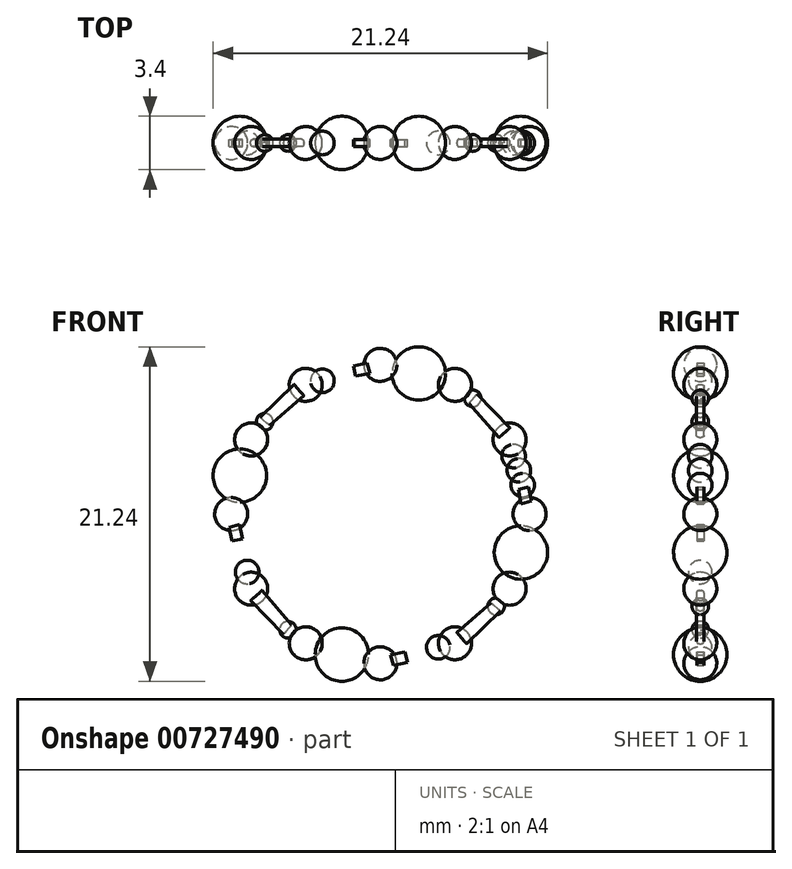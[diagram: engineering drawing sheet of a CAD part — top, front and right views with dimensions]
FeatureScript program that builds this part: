
annotation { "Feature Type Name" : "Feature", "Feature Type Description" : "" }
export const myFeature = defineFeature(function(context is Context, id is Id, definition is map)
    precondition{}
    {
        {
            var Q0;
            Q0=qCreatedBy(makeId("Front.planeOp"),FACE);
            var sketch = newSketch(context, id + "F0", { "sketchPlane" : qUnion([Q0])});
            skCircle(sketch, "E0", {"center": v(0, 0) * mm, "radius": 9 * mm});
            skSolve(sketch);
        }
        {
            var Q0;
            Q0=qCreatedBy(makeId("Front.planeOp"),FACE);
            var sketch = newSketch(context, id + "F1", { "sketchPlane" : qUnion([Q0])});
            skCircle(sketch, "E1", {"center": v(9.48, 0) * mm, "radius": 1.05 * mm});
            skLineSegment(sketch, "E2", {"start": v(9.48, 2.02) * mm, "end": v(9.48, -1.54) * mm});
            skSolve(sketch);
        }
        {
            var Q0;
            {var subQ0=sQuery(id+"F1.wireOp",EDGE,"E2");var subQ1=sQuery(id+"F1.wireOp",EDGE,"E1");var subQ2=makeQuery(id+"F1.imprint","INTERSECT",VERTEX,{"disambiguationData":[OD(0.0)],"derivedFrom":[subQ1,subQ0]});Q0=makeQuery(id+"F1.imprint","IMPRINT",FACE,{"disambiguationData":[TD([[makeQuery(id+"F1.imprint","IMPRINT",EDGE,{"disambiguationData":[TD([[subQ2,1.0]])],"derivedFrom":subQ1}),1.0]])]});}
            var Q1;
            Q1=sQuery(id+"F1.wireOp",EDGE,"E2");
            revolve(context, id + "F2", {"surfaceOperationType" : NewSurfaceOperationType.NEW, "entities" : qUnion([Q0]), "axis" : qUnion([Q1]), "revolveType" : RevolveType.FULL});
        }
        {
            var Q0;
            Q0=makeQuery(id+"F2.opRevolve","SWEPT_BODY",BODY,{"disambiguationData":[OSD([sQuery(id+"F1.wireOp",EDGE,"E1"),sQuery(id+"F1.wireOp",EDGE,"E2")])]});
            var Q1;
            Q1=sQuery(id+"F0.wireOp",EDGE,"E0");
            circularPattern(context, id + "F3", {"entities" : qUnion([Q0]), "axis" : qUnion([Q1]), "angle" : 360 * degree, "instanceCount" : 12, "equalSpace" : true});
        }
        {
            var Q0;
            Q0=qCreatedBy(makeId("Front.planeOp"),FACE);
            var sketch = newSketch(context, id + "F4", { "sketchPlane" : qUnion([Q0])});
            skCircle(sketch, "E3", {"center": v(8.93, -2.44) * mm, "radius": 1.7 * mm});
            skLineSegment(sketch, "E4", {"start": v(8.93, -0.4) * mm, "end": v(8.93, -5.01) * mm});
            skSolve(sketch);
        }
        {
            var Q0;
            {var subQ0=sQuery(id+"F4.wireOp",EDGE,"E4");var subQ1=sQuery(id+"F4.wireOp",EDGE,"E3");var subQ2=makeQuery(id+"F4.imprint","INTERSECT",VERTEX,{"disambiguationData":[OD(0.0)],"derivedFrom":[subQ1,subQ0]});Q0=makeQuery(id+"F4.imprint","IMPRINT",FACE,{"disambiguationData":[TD([[makeQuery(id+"F4.imprint","IMPRINT",EDGE,{"disambiguationData":[TD([[subQ2,1.0]])],"derivedFrom":subQ1}),1.0]])]});}
            var Q1;
            Q1=sQuery(id+"F4.wireOp",EDGE,"E4");
            revolve(context, id + "F5", {"surfaceOperationType" : NewSurfaceOperationType.NEW, "entities" : qUnion([Q0]), "axis" : qUnion([Q1]), "revolveType" : RevolveType.FULL});
        }
        {
            var Q0;
            Q0=qCreatedBy(makeId("Front.planeOp"),FACE);
            var sketch = newSketch(context, id + "F6", { "sketchPlane" : qUnion([Q0])});
            skCircle(sketch, "E5", {"center": v(9.04, 1.84) * mm, "radius": 0.75 * mm});
            skLineSegment(sketch, "E6", {"start": v(9.04, 2.84) * mm, "end": v(9.04, 0.4) * mm});
            skSolve(sketch);
        }
        {
            var Q0;
            {var subQ0=sQuery(id+"F6.wireOp",EDGE,"E6");var subQ1=sQuery(id+"F6.wireOp",EDGE,"E5");var subQ2=makeQuery(id+"F6.imprint","INTERSECT",VERTEX,{"disambiguationData":[OD(0.0)],"derivedFrom":[subQ1,subQ0]});Q0=makeQuery(id+"F6.imprint","IMPRINT",FACE,{"disambiguationData":[TD([[makeQuery(id+"F6.imprint","IMPRINT",EDGE,{"disambiguationData":[TD([[subQ2,1.0]])],"derivedFrom":subQ1}),1.0]])]});}
            var Q1;
            Q1=sQuery(id+"F6.wireOp",EDGE,"E6");
            revolve(context, id + "F7", {"operationType" : NewBodyOperationType.ADD, "surfaceOperationType" : NewSurfaceOperationType.NEW, "entities" : qUnion([Q0]), "axis" : qUnion([Q1]), "revolveType" : RevolveType.FULL});
        }
        {
            var Q0;
            Q0=makeQuery(id+"F5.opRevolve","SWEPT_BODY",BODY,{"disambiguationData":[OSD([sQuery(id+"F4.wireOp",EDGE,"E3"),sQuery(id+"F4.wireOp",EDGE,"E4")])]});
            var Q1;
            Q1=sQuery(id+"F0.wireOp",EDGE,"E0");
            circularPattern(context, id + "F8", {"entities" : qUnion([Q0]), "axis" : qUnion([Q1]), "angle" : 360 * degree, "instanceCount" : 4, "equalSpace" : true});
        }
        {
            var Q0;
            Q0=makeQuery(id+"F7.opRevolve","SWEPT_BODY",BODY,{"disambiguationData":[OSD([sQuery(id+"F6.wireOp",EDGE,"E5"),sQuery(id+"F6.wireOp",EDGE,"E6")])]});
            var Q1;
            Q1=sQuery(id+"F0.wireOp",EDGE,"E0");
            circularPattern(context, id + "F9", {"entities" : qUnion([Q0]), "axis" : qUnion([Q1]), "angle" : 12 * degree, "instanceCount" : 3, "equalSpace" : true});
        }
        {
            var Q0;
            Q0=makeQuery(id+"F9.opPattern","COPY",BODY,{"derivedFrom":makeQuery(id+"F7.opRevolve","SWEPT_BODY",BODY,{"disambiguationData":[OSD([sQuery(id+"F6.wireOp",EDGE,"E5"),sQuery(id+"F6.wireOp",EDGE,"E6")])]}),"instanceName":"2"});
            var Q1;
            Q1=sQuery(id+"F0.wireOp",EDGE,"E0");
            circularPattern(context, id + "F10", {"entities" : qUnion([Q0]), "axis" : qUnion([Q1]), "angle" : 360 * degree, "instanceCount" : 4, "equalSpace" : true});
        }
        {
            var Q0;
            Q0=qCreatedBy(makeId("Front.planeOp"),FACE);
            var sketch = newSketch(context, id + "F11", { "sketchPlane" : qUnion([Q0])});
            skCircle(sketch, "E7", {"center": v(7.35, -5.86) * mm, "radius": 0.53 * mm});
            skLineSegment(sketch, "E8", {"start": v(7.35, -4.97) * mm, "end": v(7.35, -6.96) * mm});
            skSolve(sketch);
        }
        {
            var Q0;
            {var subQ0=sQuery(id+"F11.wireOp",EDGE,"E8");var subQ1=sQuery(id+"F11.wireOp",EDGE,"E7");var subQ2=makeQuery(id+"F11.imprint","INTERSECT",VERTEX,{"disambiguationData":[OD(0.0)],"derivedFrom":[subQ1,subQ0]});Q0=makeQuery(id+"F11.imprint","IMPRINT",FACE,{"disambiguationData":[TD([[makeQuery(id+"F11.imprint","IMPRINT",EDGE,{"disambiguationData":[TD([[subQ2,-1.0]])],"derivedFrom":subQ1}),1.0]])]});}
            var Q1;
            Q1=sQuery(id+"F11.wireOp",EDGE,"E8");
            revolve(context, id + "F12", {"operationType" : NewBodyOperationType.ADD, "surfaceOperationType" : NewSurfaceOperationType.NEW, "entities" : qUnion([Q0]), "axis" : qUnion([Q1]), "revolveType" : RevolveType.FULL});
        }
        {
            var Q0;
            Q0=makeQuery(id+"F3.opPattern","COPY",BODY,{"derivedFrom":makeQuery(id+"F2.opRevolve","SWEPT_BODY",BODY,{"disambiguationData":[OSD([sQuery(id+"F1.wireOp",EDGE,"E1"),sQuery(id+"F1.wireOp",EDGE,"E2")])]}),"instanceName":"11"});
            var Q1;
            Q1=sQuery(id+"F0.wireOp",EDGE,"E0");
            circularPattern(context, id + "F13", {"entities" : qUnion([Q0]), "axis" : qUnion([Q1]), "angle" : 360 * degree, "instanceCount" : 4, "equalSpace" : true});
        }
        {
            var Q0;
            Q0=qCreatedBy(makeId("Front.planeOp"),FACE);
            var sketch = newSketch(context, id + "F14", { "sketchPlane" : qUnion([Q0])});
            skLineSegment(sketch, "E9", {"start": v(-5.64, -7.03) * mm, "end": v(-7.53, -4.86) * mm});
            skLineSegment(sketch, "E10", {"start": v(-7.53, -4.86) * mm, "end": v(-8.23, -5.48) * mm});
            skLineSegment(sketch, "E11", {"start": v(-8.23, -5.48) * mm, "end": v(-6.15, -7.64) * mm});
            skLineSegment(sketch, "E12", {"start": v(-6.15, -7.64) * mm, "end": v(-5.64, -7.03) * mm});
            skSolve(sketch);
        }
        {
            var Q0;
            Q0 = qSketchRegion(id + "F14", true);
            extrude(context, id + "F15", {"entities" : qUnion([Q0]), "endBound" : BoundingType.SYMMETRIC, "depth" : 0.48 * mm, "offsetDistance" : 25 * mm});
        }
        {
            var Q0;
            Q0=makeQuery(id+"F15.opExtrude","CAP_EDGE",EDGE,{"disambiguationData":[OSD([sQuery(id+"F14.wireOp",EDGE,"E9")])],"isStart":false});
            var Q1;
            Q1=makeQuery(id+"F15.opExtrude","CAP_EDGE",EDGE,{"disambiguationData":[OSD([sQuery(id+"F14.wireOp",EDGE,"E11")])],"isStart":false});
            var Q2;
            Q2=makeQuery(id+"F15.opExtrude","CAP_EDGE",EDGE,{"disambiguationData":[OSD([sQuery(id+"F14.wireOp",EDGE,"E9")])],"isStart":true});
            var Q3;
            Q3=makeQuery(id+"F15.opExtrude","CAP_EDGE",EDGE,{"disambiguationData":[OSD([sQuery(id+"F14.wireOp",EDGE,"E11")])],"isStart":true});
            fillet(context, id + "F16", {"entities" : qUnion([Q0, Q1, Q2, Q3]), "radius" : .2 * mm, "tangentPropagation" : true, "allowEdgeOverflow" : false});
        }
        {
            var Q0;
            Q0=makeQuery(id+"F15.opExtrude","SWEPT_BODY",BODY,{"disambiguationData":[OSD([sQuery(id+"F14.wireOp",EDGE,"E9"),sQuery(id+"F14.wireOp",EDGE,"E10"),sQuery(id+"F14.wireOp",EDGE,"E11"),sQuery(id+"F14.wireOp",EDGE,"E12")])]});
            var Q1;
            Q1=sQuery(id+"F0.wireOp",EDGE,"E0");
            circularPattern(context, id + "F17", {"entities" : qUnion([Q0]), "axis" : qUnion([Q1]), "angle" : 360 * degree, "instanceCount" : 4, "equalSpace" : true});
        }
        {
            var Q0;
            Q0=qCreatedBy(makeId("Front.planeOp"),FACE);
            var sketch = newSketch(context, id + "F18", { "sketchPlane" : qUnion([Q0])});
            skLineSegment(sketch, "E13", {"start": v(-9.6, -0.83) * mm, "end": v(-9.4, -1.72) * mm});
            skLineSegment(sketch, "E14", {"start": v(-8.77, -1.57) * mm, "end": v(-9.4, -1.72) * mm});
            skLineSegment(sketch, "E15", {"start": v(-8.94, -0.66) * mm, "end": v(-8.77, -1.57) * mm});
            skLineSegment(sketch, "E16", {"start": v(-9.6, -0.83) * mm, "end": v(-8.94, -0.66) * mm});
            skSolve(sketch);
        }
        {
            var Q0;
            Q0=makeQuery(id+"F18.imprint","IMPRINT",FACE,{"disambiguationData":[TD([[makeQuery(id+"F18.imprint","IMPRINT",EDGE,{"derivedFrom":sQuery(id+"F18.wireOp",EDGE,"E13")}),1.0]])]});
            extrude(context, id + "F19", {"entities" : qUnion([Q0]), "endBound" : BoundingType.SYMMETRIC, "depth" : 0.44 * mm, "offsetDistance" : 25 * mm});
        }
        {
            var Q0;
            Q0=makeQuery(id+"F19.opExtrude","SWEPT_BODY",BODY,{"disambiguationData":[OSD([sQuery(id+"F18.wireOp",EDGE,"E13"),sQuery(id+"F18.wireOp",EDGE,"E14"),sQuery(id+"F18.wireOp",EDGE,"E15"),sQuery(id+"F18.wireOp",EDGE,"E16")])]});
            var Q1;
            Q1=sQuery(id+"F0.wireOp",EDGE,"E0");
            circularPattern(context, id + "F20", {"entities" : qUnion([Q0]), "axis" : qUnion([Q1]), "angle" : 360 * degree, "instanceCount" : 4, "equalSpace" : true});
        }
    });
